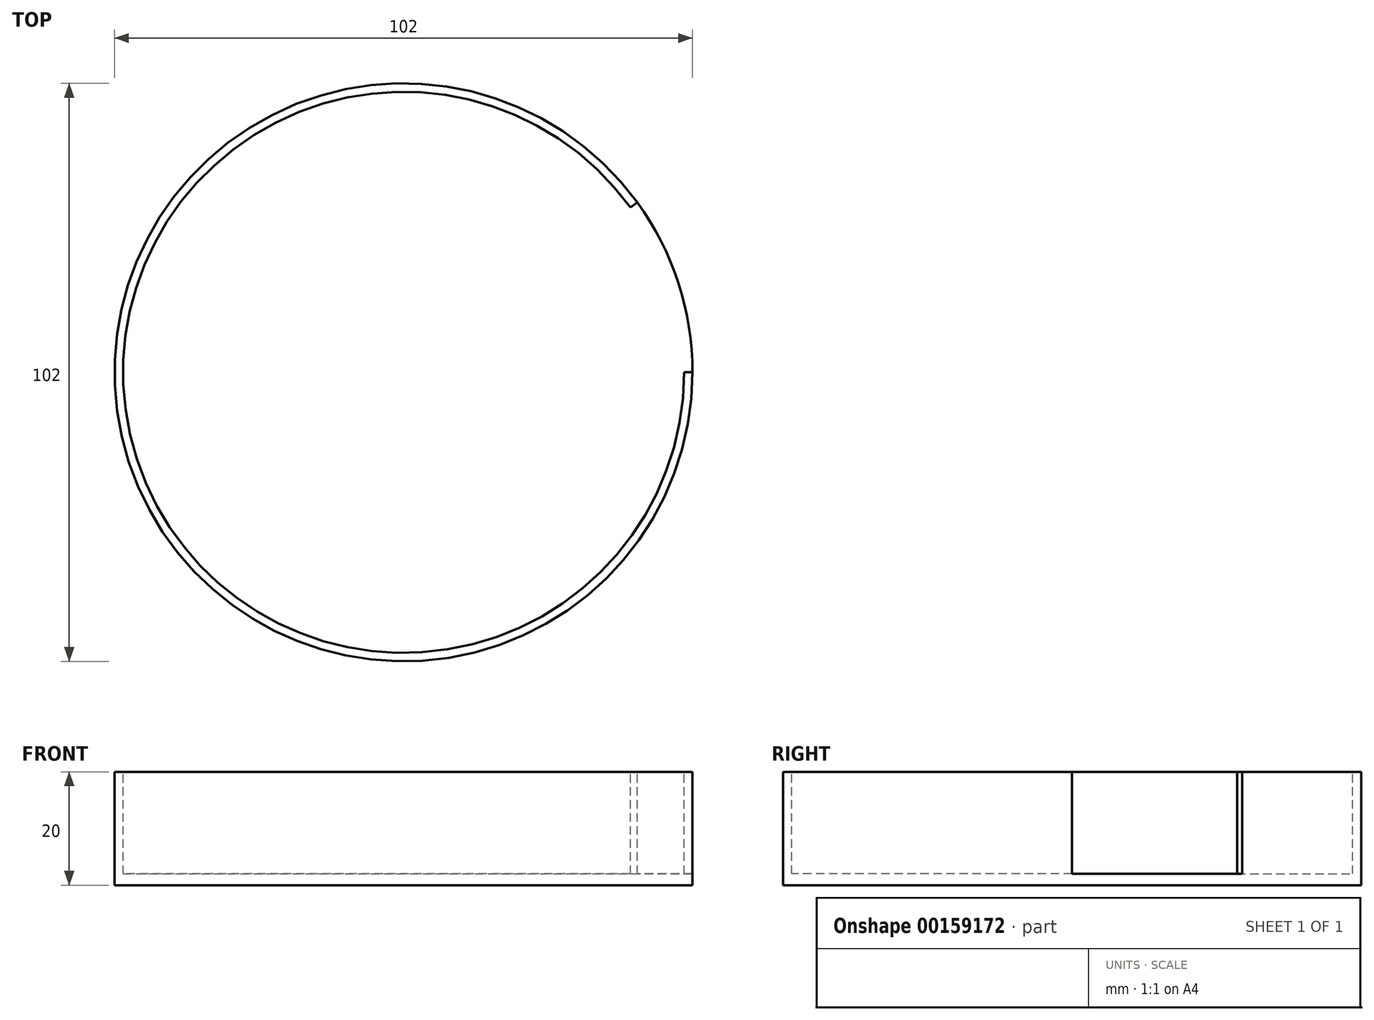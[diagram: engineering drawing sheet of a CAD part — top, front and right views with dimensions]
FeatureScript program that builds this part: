
annotation { "Feature Type Name" : "Feature", "Feature Type Description" : "" }
export const myFeature = defineFeature(function(context is Context, id is Id, definition is map)
    precondition{}
    {
        {
            var Q0;
            Q0=qCreatedBy(makeId("Top.planeOp"),FACE);
            var sketch = newSketch(context, id + "F0", { "sketchPlane" : qUnion([Q0])});
            skCircle(sketch, "E0", {"center": v(0, 0) * mm, "radius": 51 * mm});
            skSolve(sketch);
        }
        {
            var Q0;
            Q0 = qSketchRegion(id + "F0", true);
            extrude(context, id + "F1", {"entities" : qUnion([Q0]), "depth" : 20 * mm});
        }
        {
            var Q0;
            Q0=makeQuery(id+"F1.opExtrude","CAP_FACE",FACE,{"disambiguationData":[OSD([sQuery(id+"F0.wireOp",EDGE,"E0")])],"isStart":false});
            var sketch = newSketch(context, id + "F2", { "sketchPlane" : qUnion([Q0])});
            skCircle(sketch, "E1", {"center": v(0, 0) * mm, "radius": 49.5 * mm});
            skLineSegment(sketch, "E2", {"start": v(0, 0) * mm, "end": v(51, 0) * mm});
            skLineSegment(sketch, "E3", {"start": v(0, 0) * mm, "end": v(41.26, 29.98) * mm});
            skArc(sketch, "E4", {"start": v(51, 0) * mm, "mid": v(48.5, 15.76) * mm, "end": v(41.26, 29.98) * mm});
            skSolve(sketch);
        }
        {
            var Q0;
            Q0 = qSketchRegion(id + "F2", true);
            extrude(context, id + "F3", {"entities" : qUnion([Q0]), "operationType" : NewBodyOperationType.REMOVE, "oppositeDirection" : true, "depth" : 18 * mm});
        }
    });
